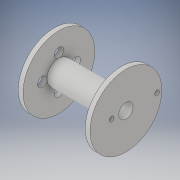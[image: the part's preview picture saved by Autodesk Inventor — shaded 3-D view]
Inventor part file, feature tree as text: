
AUTODESK INVENTOR PART (.ipt)
format: ipt  version: 2019 (Build 230136000, 136)  size: 148,992 bytes
history: native  units: in
note: dims shown in document units (in); Inventor stores cm internally (conversion verified against a paired STEP export)
features: sketch x3, extrude x2, revolve x1
ambient origin geometry x8: Origin, YZ Plane, XZ Plane, XY Plane, X Axis, Y Axis, Z Axis, Center Point
bodies: Solid1 (feature_tree)
feature tree (6):
  revolve  "Revolution1"  [1 undecoded]
  sketch  "Sketch2"  dims[d2=1.0236in d3=0.0787in]
  extrude  "Extrusion1"  Depth=0.0787in
  extrude  "Extrusion2"  Depth=0.1181in
  sketch  "Sketch1"  dims[d0=0.0787in d1=0.3937in]
  sketch  "Sketch4"  dims[d4=0.4724in d5=0.1181in d6=1.1811in d7=90.0deg d8=0.1575in d10=0.1575in d13=0.1575in d14=0.1575in d17=0.2756in d18=0.2756in d19=0.2756in d20=0.2756in d21=0.0787in d22=0.0in d23=0.0787in d24=0.0787in d25=0.2362in d26=0.5118in d27=0.0787in d28=0.0in d30=0.0787in]
note: 1 required parameter value undecoded (feature->parameter linkage not recoverable at this tier; creation-order binding heuristic only, values carry confidence <= 0.55)
